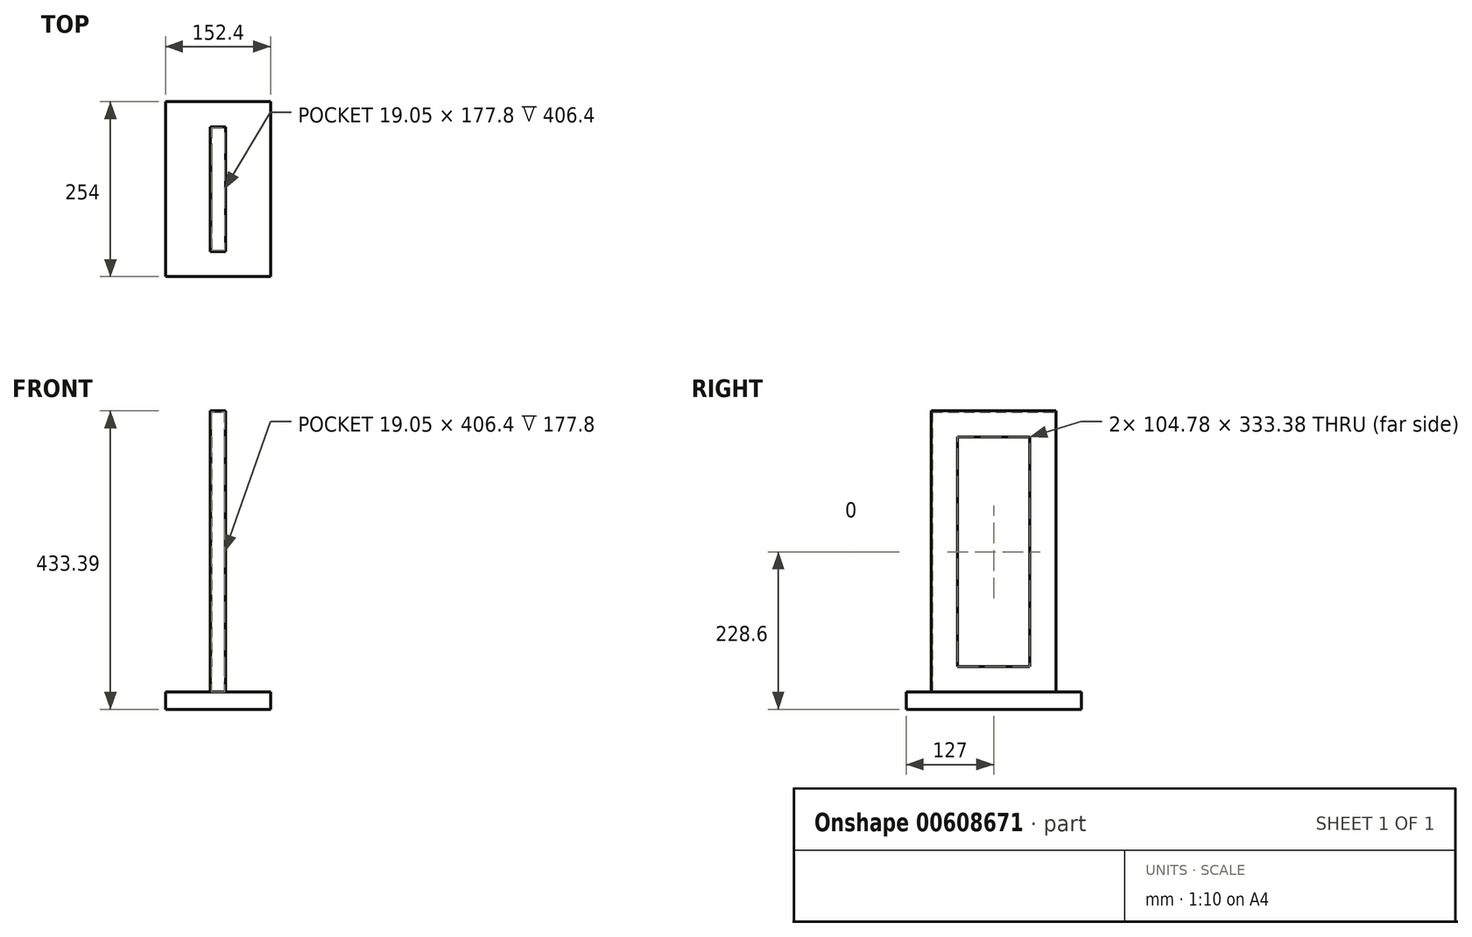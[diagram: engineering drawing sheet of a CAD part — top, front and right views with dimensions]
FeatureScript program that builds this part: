
annotation { "Feature Type Name" : "Feature", "Feature Type Description" : "" }
export const myFeature = defineFeature(function(context is Context, id is Id, definition is map)
    precondition{}
    {
        {
            var Q0;
            Q0=qCreatedBy(makeId("Right.planeOp"),FACE);
            var sketch = newSketch(context, id + "F0", { "sketchPlane" : qUnion([Q0])});
            skLineSegment(sketch, "E0.bottom", {"start": v(38.1, 76.2) * mm, "end": v(-38.1, 76.2) * mm});
            skLineSegment(sketch, "E0.top", {"start": v(38.1, 381) * mm, "end": v(-38.1, 381) * mm});
            skLineSegment(sketch, "E0.left", {"start": v(38.1, 76.2) * mm, "end": v(38.1, 381) * mm});
            skLineSegment(sketch, "E0.right", {"start": v(-38.1, 76.2) * mm, "end": v(-38.1, 381) * mm});
            skPoint(sketch, "E0.middle", {"position": v(0, 228.6) * mm});
            skLineSegment(sketch, "E1.bottom", {"start": v(88.9, 25.4) * mm, "end": v(-88.9, 25.4) * mm});
            skLineSegment(sketch, "E1.top", {"start": v(88.9, 431.8) * mm, "end": v(-88.9, 431.8) * mm});
            skLineSegment(sketch, "E1.left", {"start": v(88.9, 25.4) * mm, "end": v(88.9, 431.8) * mm});
            skLineSegment(sketch, "E1.right", {"start": v(-88.9, 25.4) * mm, "end": v(-88.9, 431.8) * mm});
            skLineSegment(sketch, "E2.bottom", {"start": v(-127, 0) * mm, "end": v(127, 0) * mm});
            skLineSegment(sketch, "E2.top", {"start": v(-127, 25.4) * mm, "end": v(127, 25.4) * mm});
            skLineSegment(sketch, "E2.left", {"start": v(-127, 0) * mm, "end": v(-127, 25.4) * mm});
            skLineSegment(sketch, "E2.right", {"start": v(127, 0) * mm, "end": v(127, 25.4) * mm});
            skPoint(sketch, "E2.middle", {"position": v(0, 12.7) * mm});
            skSolve(sketch);
        }
        {
            var Q0;
            Q0=makeQuery(id+"F0.imprint","IMPRINT",FACE,{"disambiguationData":[TD([[makeQuery(id+"F0.imprint","IMPRINT",EDGE,{"derivedFrom":sQuery(id+"F0.wireOp",EDGE,"E0.bottom")}),1.0]])]});
            var Q1;
            Q1=makeQuery(id+"F0.imprint","IMPRINT",FACE,{"disambiguationData":[TD([[makeQuery(id+"F0.imprint","IMPRINT",EDGE,{"derivedFrom":sQuery(id+"F0.wireOp",EDGE,"E0.bottom")}),-1.0]])]});
            extrude(context, id + "F1", {"entities" : qUnion([Q0, Q1]), "endBound" : BoundingType.SYMMETRIC, "depth" : 19.05 * mm, "offsetDistance" : 25.4 * mm});
        }
        {
            var Q0;
            Q0=makeQuery(id+"F0.imprint","IMPRINT",FACE,{"disambiguationData":[TD([[makeQuery(id+"F0.imprint","IMPRINT",EDGE,{"derivedFrom":sQuery(id+"F0.wireOp",EDGE,"E2.bottom")}),1.0]])]});
            extrude(context, id + "F2", {"entities" : qUnion([Q0]), "endBound" : BoundingType.SYMMETRIC, "depth" : 152.4 * mm, "offsetDistance" : 25.4 * mm});
        }
        {
            var Q0;
            Q0=makeQuery(id+"F2.opExtrude","SWEPT_FACE",FACE,{"disambiguationData":[OSD([sQuery(id+"F0.wireOp",EDGE,"E2.top")])]});
            var sketch = newSketch(context, id + "F3", { "sketchPlane" : qUnion([Q0])});
            skLineSegment(sketch, "E3.0.0", {"start": v(-9.53, 88.9) * mm, "end": v(-9.53, -88.9) * mm, "construction": true});
            skLineSegment(sketch, "E3.0.1", {"start": v(-9.52, -88.9) * mm, "end": v(9.53, -88.9) * mm, "construction": true});
            skLineSegment(sketch, "E3.0.2", {"start": v(9.53, -88.9) * mm, "end": v(9.53, 88.9) * mm, "construction": true});
            skLineSegment(sketch, "E3.0.3", {"start": v(9.53, 88.9) * mm, "end": v(-9.52, 88.9) * mm, "construction": true});
            skLineSegment(sketch, "E4", {"start": v(-9.52, -88.9) * mm, "end": v(-9.53, -52.39) * mm});
            skLineSegment(sketch, "E5", {"start": v(-9.53, -52.39) * mm, "end": v(-11.11, -52.39) * mm});
            skLineSegment(sketch, "E6", {"start": v(-11.11, -52.39) * mm, "end": v(-11.11, -90.49) * mm});
            skLineSegment(sketch, "E7", {"start": v(-11.11, -90.49) * mm, "end": v(11.11, -90.49) * mm});
            skLineSegment(sketch, "E8", {"start": v(11.11, -90.49) * mm, "end": v(11.11, -52.39) * mm});
            skLineSegment(sketch, "E9", {"start": v(11.11, -52.39) * mm, "end": v(9.52, -52.39) * mm});
            skLineSegment(sketch, "E10", {"start": v(9.53, -52.39) * mm, "end": v(9.53, -88.9) * mm});
            skLineSegment(sketch, "E11", {"start": v(9.53, -88.9) * mm, "end": v(9.53, 88.9) * mm});
            skLineSegment(sketch, "E12", {"start": v(-9.53, -88.9) * mm, "end": v(9.53, -88.9) * mm});
            skSolve(sketch);
        }
        {
            var Q0;
            Q0=makeQuery(id+"F3.imprint","IMPRINT",FACE,{"disambiguationData":[TD([[makeQuery(id+"F3.imprint","IMPRINT",EDGE,{"derivedFrom":sQuery(id+"F3.wireOp",EDGE,"E4")}),1.0]])]});
            var Q1;
            Q1=makeQuery(id+"F1.opExtrude","CAP_EDGE",EDGE,{"disambiguationData":[OSD([sQuery(id+"F0.wireOp",EDGE,"E1.right")])],"isStart":false});
            var Q2;
            Q2=makeQuery(id+"F1.opExtrude","CAP_EDGE",EDGE,{"disambiguationData":[OSD([sQuery(id+"F0.wireOp",EDGE,"E1.top")])],"isStart":false});
            var Q3;
            Q3=makeQuery(id+"F1.opExtrude","CAP_EDGE",EDGE,{"disambiguationData":[OSD([sQuery(id+"F0.wireOp",EDGE,"E1.left")])],"isStart":false});
            var Q4;
            Q4=sQuery(id+"F3.wireOp",EDGE,"E11");
            sweep(context, id + "F4", {"profiles" : qUnion([Q0]), "path" : qUnion([Q1, Q2, Q3, Q4])});
        }
    });
